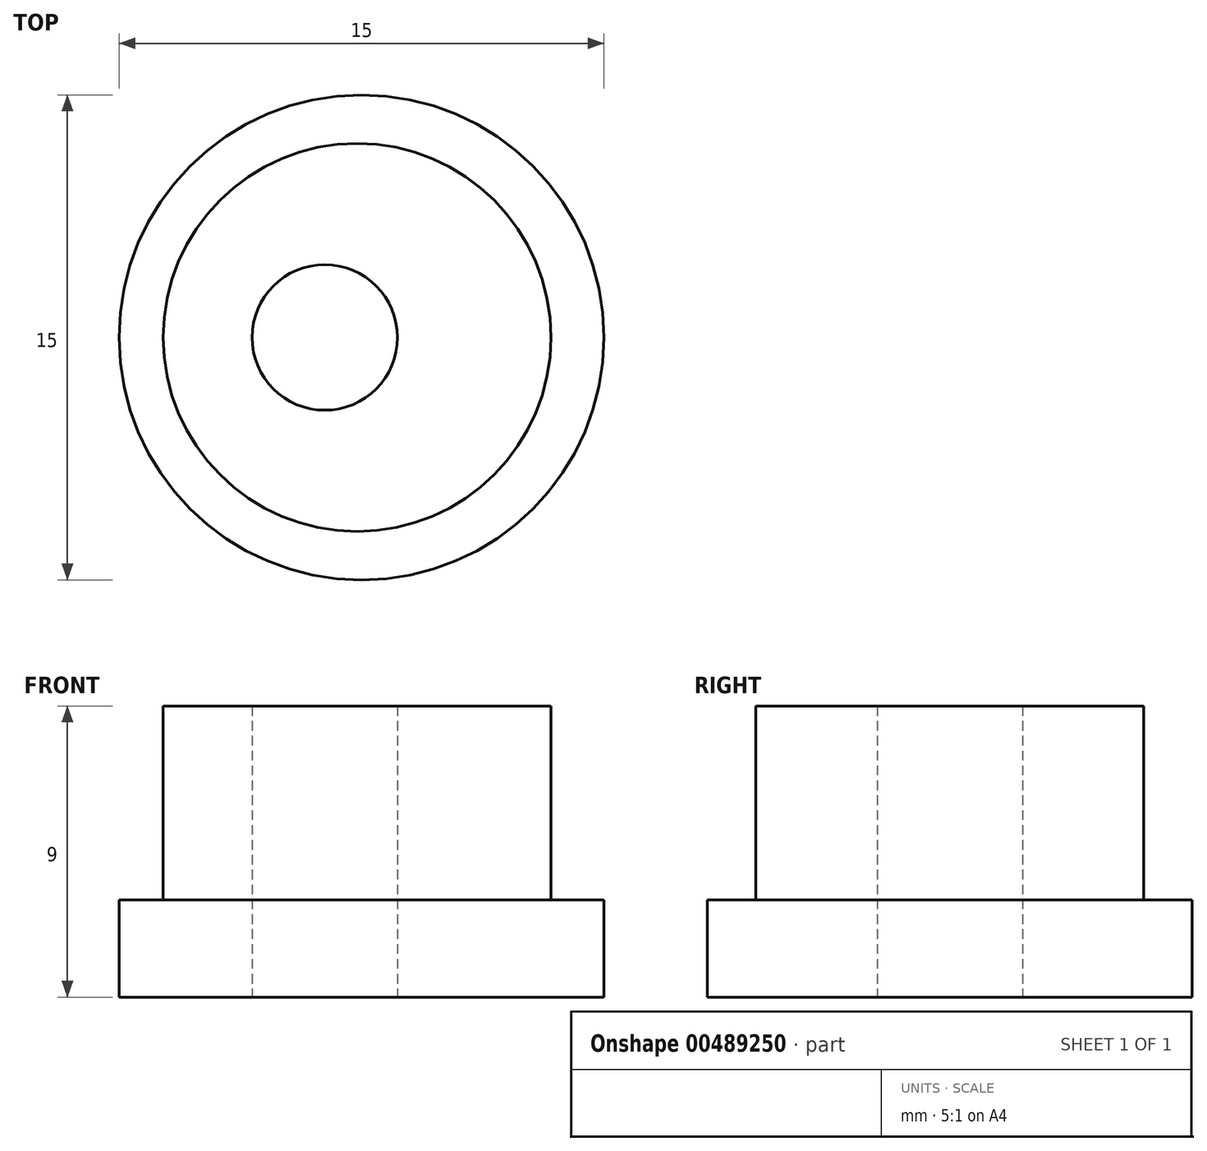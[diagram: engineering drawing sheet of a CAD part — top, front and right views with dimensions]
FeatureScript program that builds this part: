
annotation { "Feature Type Name" : "Feature", "Feature Type Description" : "" }
export const myFeature = defineFeature(function(context is Context, id is Id, definition is map)
    precondition{}
    {
        {
            var Q0;
            Q0=qCreatedBy(makeId("Top.planeOp"),FACE);
            var sketch = newSketch(context, id + "F0", { "sketchPlane" : qUnion([Q0])});
            skCircle(sketch, "E0", {"center": v(0, 0) * mm, "radius": 2.25 * mm});
            skLineSegment(sketch, "E1", {"start": v(0, 0) * mm, "end": v(1, 0) * mm});
            skCircle(sketch, "E2", {"center": v(1, 0) * mm, "radius": 6 * mm});
            skSolve(sketch);
        }
        {
            var Q0;
            Q0=makeQuery(id+"F0.imprint","IMPRINT",FACE,{"disambiguationData":[TD([[makeQuery(id+"F0.imprint","IMPRINT",EDGE,{"derivedFrom":sQuery(id+"F0.wireOp",EDGE,"E0")}),-1.0]])]});
            extrude(context, id + "F1", {"entities" : qUnion([Q0]), "depth" : 6 * mm});
        }
        {
            var Q0;
            Q0=makeQuery(id+"F0.imprint","IMPRINT",FACE,{"disambiguationData":[TD([[makeQuery(id+"F0.imprint","IMPRINT",EDGE,{"derivedFrom":sQuery(id+"F0.wireOp",EDGE,"E0")}),-1.0]])]});
            var sketch = newSketch(context, id + "F2", { "sketchPlane" : qUnion([Q0])});
            skCircle(sketch, "E3", {"center": v(1.14, 0) * mm, "radius": 7.5 * mm});
            skSolve(sketch);
        }
        {
            var Q0;
            Q0=makeQuery(id+"F2.imprint","IMPRINT",FACE,{"disambiguationData":[TD([[makeQuery(id+"F2.imprint","IMPRINT",EDGE,{"derivedFrom":sQuery(id+"F2.wireOp",EDGE,"E3")}),1.0]])]});
            var Q1;
            Q1=makeQuery(id+"F0.imprint","IMPRINT",FACE,{"disambiguationData":[TD([[makeQuery(id+"F0.imprint","IMPRINT",EDGE,{"derivedFrom":sQuery(id+"F0.wireOp",EDGE,"E0")}),-1.0]])]});
            extrude(context, id + "F3", {"entities" : qUnion([Q0, Q1]), "operationType" : NewBodyOperationType.ADD, "oppositeDirection" : true, "depth" : 3 * mm});
        }
    });
